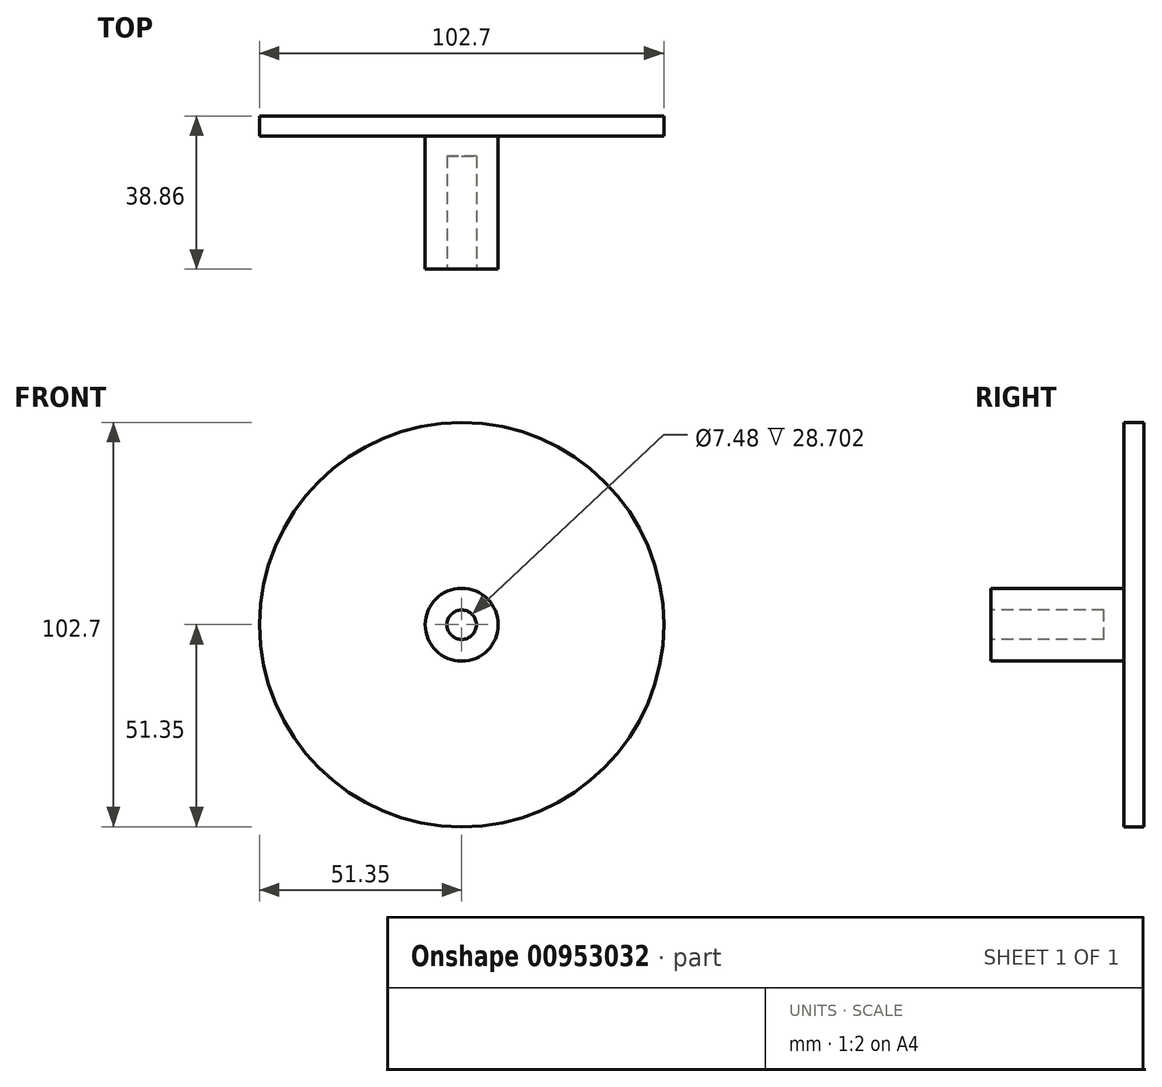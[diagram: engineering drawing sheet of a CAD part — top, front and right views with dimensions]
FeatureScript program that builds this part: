
annotation { "Feature Type Name" : "Feature", "Feature Type Description" : "" }
export const myFeature = defineFeature(function(context is Context, id is Id, definition is map)
    precondition{}
    {
        {
            var Q0;
            Q0=qCreatedBy(makeId("Front.planeOp"),FACE);
            var sketch = newSketch(context, id + "F0", { "sketchPlane" : qUnion([Q0])});
            skCircle(sketch, "E0", {"center": v(0, 0) * mm, "radius": 51.35 * mm});
            skSolve(sketch);
        }
        {
            var Q0;
            Q0=makeQuery(id+"F0.imprint","IMPRINT",FACE,{"disambiguationData":[TD([[makeQuery(id+"F0.imprint","IMPRINT",EDGE,{"derivedFrom":sQuery(id+"F0.wireOp",EDGE,"E0")}),1.0]])]});
            extrude(context, id + "F1", {"entities" : qUnion([Q0]), "depth" : 5.08 * mm, "offsetDistance" : 25.4 * mm});
        }
        {
            var Q0;
            Q0=qCreatedBy(makeId("Front.planeOp"),FACE);
            var sketch = newSketch(context, id + "F2", { "sketchPlane" : qUnion([Q0])});
            skCircle(sketch, "E1", {"center": v(0, 0) * mm, "radius": 9.27 * mm});
            skSolve(sketch);
        }
        {
            var Q0;
            Q0 = qSketchRegion(id + "F2", true);
            extrude(context, id + "F3", {"entities" : qUnion([Q0]), "operationType" : NewBodyOperationType.ADD, "depth" : 38.86 * mm, "offsetDistance" : 25.4 * mm});
        }
        {
            var Q0;
            Q0=makeQuery(id+"F3.opExtrude","CAP_FACE",FACE,{"disambiguationData":[OSD([sQuery(id+"F2.wireOp",EDGE,"E1")])],"isStart":false});
            var sketch = newSketch(context, id + "F4", { "sketchPlane" : qUnion([Q0])});
            skCircle(sketch, "E2", {"center": v(0, 0) * mm, "radius": 3.74 * mm});
            skSolve(sketch);
        }
        {
            var Q0;
            Q0=makeQuery(id+"F4.imprint","IMPRINT",FACE,{"disambiguationData":[TD([[makeQuery(id+"F4.imprint","IMPRINT",EDGE,{"derivedFrom":sQuery(id+"F4.wireOp",EDGE,"E2")}),1.0]])]});
            extrude(context, id + "F5", {"entities" : qUnion([Q0]), "operationType" : NewBodyOperationType.REMOVE, "oppositeDirection" : true, "depth" : 28.7 * mm, "offsetDistance" : 25.4 * mm});
        }
        {
            var Q0;
            Q0=qCreatedBy(makeId("Front.planeOp"),FACE);
            cPlane(context, id + "F6", {"entities" : qUnion([Q0]), "cplaneType" : CPlaneType.OFFSET, "offset" : 12.45 * mm, "width" : 152.4 * mm, "height" : 152.4 * mm});
        }
        {
            var Q0;
            Q0=qCreatedBy(id+"F6.planeOp",FACE);
            cPlane(context, id + "F7", {"entities" : qUnion([Q0]), "cplaneType" : CPlaneType.OFFSET, "offset" : 13.97 * mm, "width" : 152.4 * mm, "height" : 152.4 * mm});
        }
        {
            var Q0;
            Q0=qCreatedBy(makeId("Front.planeOp"),FACE);
            cPlane(context, id + "F8", {"entities" : qUnion([Q0]), "cplaneType" : CPlaneType.OFFSET, "offset" : 36.83 * mm, "width" : 152.4 * mm, "height" : 152.4 * mm});
        }
    });
